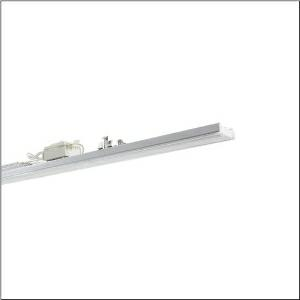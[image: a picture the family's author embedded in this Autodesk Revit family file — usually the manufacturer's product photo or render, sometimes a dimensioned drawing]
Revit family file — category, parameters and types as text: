
# Revit family: licross_r__21_recessed_mo_52tl18vn465g_e7ea
name_source: partatom
category: Lighting Fixtures
units: mm (PartAtom-declared; Revit-internal decimal feet)

## family parameters
Cut with Voids When Loaded = No
Host = Face
Light Source = No
Part Type = Normal
Room Calculation Point = No
Round Connector Dimension = Use Diameter
Shared = No

## types (1)
- --- (1 x LED, 6500 lm, 36.8 W, 4000K)
    Apparent Load = 37 VA
    CIE Flux Codes = 79 95 99 100 100
    Color Rendering = 80
    Color Temperature = 4000K
    Default Elevation = 1800 mm
    Description = Licross® 21 Recessed MO, luminaire insert, of sheet steel, galvanised, coil coated, white, length: 1.500mm, width: 66mm, height: 67mm, LED rated luminous flux: 6.500lm, light colour: 840, control gear: DALI 2, CLO, with plug, 5-pole, with phase selection, mains connection: 220..240V, AC, 50/60Hz, start of lifetime: 37W, end of service life: 44W, internal wiring halogen-free, primary optical cover: cover, of PMMA, light emission: direct distribution, primary light characteristic: symmetric, protection rating (complete): IP40, insulation class (complete): insulation class I (protective earthing), certification: CE, ENEC, VDE, UKCA, protection symbol: D if used in an environment without relevant dust loads with corresponding accessories, impact resistance: IK06, permissible ambient temperature for indoor applications: -25..+40°C, corresponds to IFS (International Featured Standards) requirements for safety and quality in the food industry, reducing of maximum allowable ambient temperature of 5°C with ceiling mounting, LABS conformity tested according to VDMA 24364:2018-05, packaging unit: 1 piece
    Height = 58 mm
    Lamp = 1 x LED
    Lamp Light Flux = 6500 lm
    Lamp Power = 36.8 W
    Lamp count = 1
    Length = 1500 mm
    Luminous efficacy = 177 lm/W
    Manufacturer = Siteco
    ModVariant = No
    Model = 52TL18VN465G
    Mounting Place = Ceiling
    Mounting Type = Pendant
    Number of Poles = 1
    OnlyDefault = Yes
    Power Factor = 1
    Product Name = Licross® 21 Recessed MO
    Product group = luminaire insert | ceiling pendant
    ProductGroupID = 902
    Protection Class = Protection class I
    Protection Degree = IP 40
    RLX_Detail_Level = 1
    RLX_Emergency_Light_Flux = 0 lm
    RLX_Emergency_Type = 0
    RLX_Emergency_Type_DB = No
    RlxData = <blob elided: 24697 chars, md5=748668de>
    Socket = socket
    Standby Power = 0 W
    System Light Flux = 6500 lm
    System Power = 37 W
    Type Comments = factory setting: luminous flux: 100 % | dim-lin: 254 | 246 mA
    Type Image = l_1296930.jpg
    URL = http://relux.com
    VarID = @adj_103753
    Voltage = 0 V
    Weight = 0.00 kg
    Width = 66 mm

## geometry (parser evidence)
native form markers: Blend x4, Sweep x12
no freeform markers — native parametric forms only
